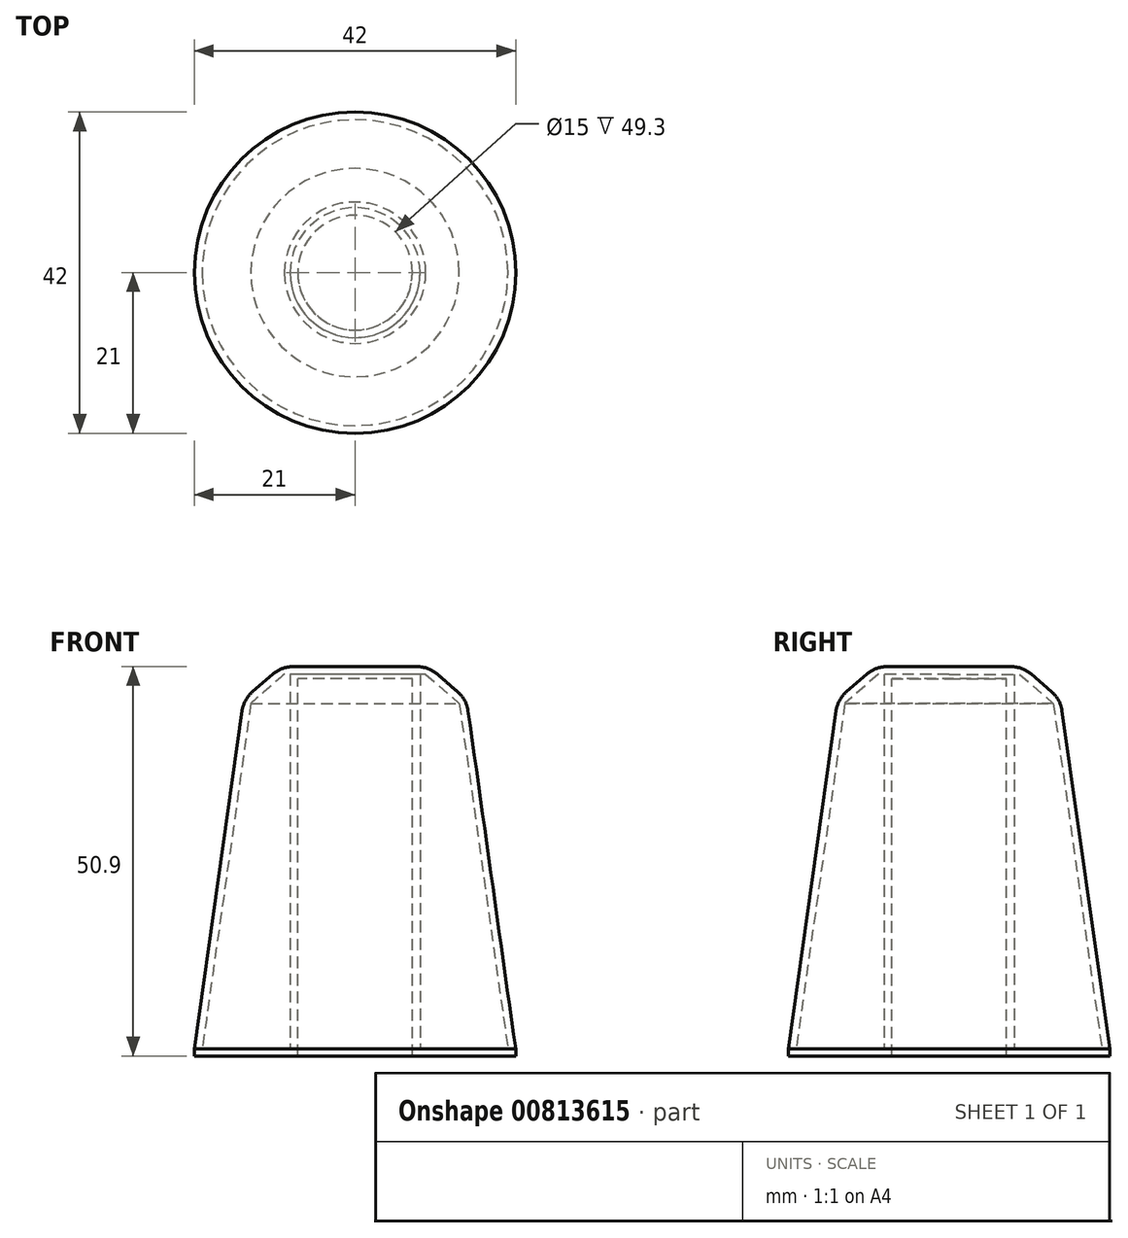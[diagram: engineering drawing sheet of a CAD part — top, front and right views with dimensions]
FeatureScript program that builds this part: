
annotation { "Feature Type Name" : "Feature", "Feature Type Description" : "" }
export const myFeature = defineFeature(function(context is Context, id is Id, definition is map)
    precondition{}
    {
        {
            assignVariable(context, id + "F0", {"name" : "Height", "anyValue" : 50});
        }
        {
            var Q0;
            Q0=qCreatedBy(makeId("Top.planeOp"),FACE);
            var sketch = newSketch(context, id + "F1", { "sketchPlane" : qUnion([Q0])});
            skCircle(sketch, "E0", {"center": v(0, 0) * mm, "radius": 21 * mm});
            skSolve(sketch);
        }
        {
            var Q0;
            Q0=qCreatedBy(makeId("Top.planeOp"),FACE);
            cPlane(context, id + "F2", {"entities" : qUnion([Q0]), "cplaneType" : CPlaneType.OFFSET, "offset" : (getVariable(context, 'Height')) * mm, "width" : 150 * mm, "height" : 150 * mm});
        }
        {
            var Q0;
            Q0=qCreatedBy(id+"F2.planeOp",FACE);
            var sketch = newSketch(context, id + "F3", { "sketchPlane" : qUnion([Q0])});
            skCircle(sketch, "E1", {"center": v(0, 0) * mm, "radius": 13.96 * mm});
            skSolve(sketch);
        }
        {
            var Q0;
            Q0=makeQuery(id+"F1.imprint","IMPRINT",FACE,{"disambiguationData":[TD([[makeQuery(id+"F1.imprint","IMPRINT",EDGE,{"derivedFrom":sQuery(id+"F1.wireOp",EDGE,"E0")}),1.0]])]});
            var Q1;
            Q1=makeQuery(id+"F3.imprint","IMPRINT",FACE,{"disambiguationData":[TD([[makeQuery(id+"F3.imprint","IMPRINT",EDGE,{"derivedFrom":sQuery(id+"F3.wireOp",EDGE,"E1")}),1.0]])]});
            loft(context, id + "F4", {"sheetProfilesArray" : [{ "sheetProfileEntities" : qUnion([Q0]) }, { "sheetProfileEntities" : qUnion([Q1]) }]});
        }
        {
            var Q0;
            Q0=makeQuery(id+"F4.opLoft","CAP_FACE",FACE,{"disambiguationData":[OSD([makeQuery(id+"F1.imprint","IMPRINT",FACE,{"disambiguationData":[TD([[makeQuery(id+"F1.imprint","IMPRINT",EDGE,{"derivedFrom":sQuery(id+"F1.wireOp",EDGE,"E0")}),1.0]])]})])],"isStart":true});
            var sketch = newSketch(context, id + "F5", { "sketchPlane" : qUnion([Q0])});
            skCircle(sketch, "E2", {"center": v(0, 0) * mm, "radius": 7.5 * mm});
            skSolve(sketch);
        }
        {
            var Q0;
            Q0=makeQuery(id+"F4.opLoft","MID_CAP_EDGE",EDGE,{"disambiguationData":[OSD([sQuery(id+"F3.wireOp",EDGE,"E1")])],"capPos":1.0});
            chamfer(context, id + "F6", {"entities" : qUnion([Q0]), "width" : 5 * mm, "tangentPropagation" : true});
        }
        {
            var Q0;
            Q0=makeQuery(id+"F4.opLoft","CAP_FACE",FACE,{"disambiguationData":[OSD([makeQuery(id+"F1.imprint","IMPRINT",FACE,{"disambiguationData":[TD([[makeQuery(id+"F1.imprint","IMPRINT",EDGE,{"derivedFrom":sQuery(id+"F1.wireOp",EDGE,"E0")}),1.0]])]})])],"isStart":true});
            shell(context, id + "F7", {"entities" : qUnion([Q0]), "thickness" : 1 * mm});
        }
        {
            var Q0;
            Q0=makeQuery(id+"F5.imprint","IMPRINT",FACE,{"disambiguationData":[TD([[makeQuery(id+"F5.imprint","IMPRINT",EDGE,{"derivedFrom":sQuery(id+"F5.wireOp",EDGE,"E2")}),-1.0]])]});
            extrude(context, id + "F8", {"entities" : qUnion([Q0]), "operationType" : NewBodyOperationType.ADD, "depth" : 0.9 * mm, "offsetDistance" : 25 * mm});
        }
        {
            var Q0;
            {var subQ0=sQuery(id+"F3.wireOp",EDGE,"E1");Q0=makeQuery(id+"F6.opChamfer","BLEND_EDGE",EDGE,{"blendedFrom":[makeQuery(id+"F4.opLoft","MID_CAP_EDGE",EDGE,{"disambiguationData":[OSD([subQ0])],"capPos":1.0}),makeQuery(id+"F4.opLoft","CAP_FACE",FACE,{"disambiguationData":[OSD([makeQuery(id+"F3.imprint","IMPRINT",FACE,{"disambiguationData":[TD([[makeQuery(id+"F3.imprint","IMPRINT",EDGE,{"derivedFrom":subQ0}),1.0]])]})])],"isStart":true})],"blendedInto":[makeQuery(id+"F4.opLoft","CAP_FACE",FACE,{"disambiguationData":[OSD([makeQuery(id+"F3.imprint","IMPRINT",FACE,{"disambiguationData":[TD([[makeQuery(id+"F3.imprint","IMPRINT",EDGE,{"derivedFrom":subQ0}),1.0]])]})])],"isStart":true})]});}
            var Q1;
            {var subQ0=sQuery(id+"F3.wireOp",EDGE,"E1");Q1=makeQuery(id+"F6.opChamfer","BLEND_EDGE",EDGE,{"blendedFrom":[makeQuery(id+"F4.opLoft","MID_CAP_EDGE",EDGE,{"disambiguationData":[OSD([subQ0])],"capPos":1.0}),makeQuery(id+"F4.opLoft","SWEPT_FACE",FACE,{"disambiguationData":[OSD([sQuery(id+"F1.wireOp",EDGE,"E0"),subQ0])]})],"blendedInto":[makeQuery(id+"F4.opLoft","SWEPT_FACE",FACE,{"disambiguationData":[OSD([sQuery(id+"F1.wireOp",EDGE,"E0"),subQ0])]})]});}
            fillet(context, id + "F9", {"entities" : qUnion([Q0, Q1]), "radius" : 4 * mm, "tangentPropagation" : true, "allowEdgeOverflow" : false});
        }
        {
            var Q0;
            Q0=makeQuery(id+"F8.opExtrude","CAP_FACE",FACE,{"disambiguationData":[OSD([sQuery(id+"F1.wireOp",EDGE,"E0"),sQuery(id+"F5.wireOp",EDGE,"E2")])],"isStart":false});
            var sketch = newSketch(context, id + "F10", { "sketchPlane" : qUnion([Q0])});
            skCircle(sketch, "E3.0", {"center": v(0, 0) * mm, "radius": 8.5 * mm});
            skCircle(sketch, "E4.0", {"center": v(0, 0) * mm, "radius": 16 * mm});
            skSolve(sketch);
        }
        {
            var Q0;
            Q0=makeQuery(id+"F10.imprint","IMPRINT",FACE,{"disambiguationData":[TD([[makeQuery(id+"F10.imprint","IMPRINT",EDGE,{"derivedFrom":sQuery(id+"F10.wireOp",EDGE,"E3.0")}),1.0]])]});
            var Q1;
            Q1=makeQuery(id+"F7.opShell","OFFSET_FACE",FACE,{"disambiguationData":[OSD([makeQuery(id+"F3.imprint","IMPRINT",FACE,{"disambiguationData":[TD([[makeQuery(id+"F3.imprint","IMPRINT",EDGE,{"derivedFrom":sQuery(id+"F3.wireOp",EDGE,"E1")}),1.0]])]})])]});
            extrude(context, id + "F11", {"entities" : qUnion([Q0]), "operationType" : NewBodyOperationType.ADD, "endBound" : BoundingType.UP_TO_SURFACE, "oppositeDirection" : true, "depth" : 25 * mm, "endBoundEntityFace" : qUnion([Q1]), "offsetDistance" : 25 * mm});
        }
        {
            var Q0;
            {var subQ0=sQuery(id+"F5.wireOp",EDGE,"E2");Q0=makeQuery(id+"F11.boolean.opBoolean","SPLIT",FACE,{"disambiguationData":[TD([makeQuery(id+"F8.opExtrude","SWEPT_FACE",FACE,{"disambiguationData":[OSD([subQ0])]})])],"derivedFrom":makeQuery(id+"F7.opShell","OFFSET_FACE",FACE,{"disambiguationData":[OSD([makeQuery(id+"F3.imprint","IMPRINT",FACE,{"disambiguationData":[TD([[makeQuery(id+"F3.imprint","IMPRINT",EDGE,{"derivedFrom":sQuery(id+"F3.wireOp",EDGE,"E1")}),1.0]])]})])]})});}
            extrude(context, id + "F12", {"entities" : qUnion([Q0]), "operationType" : NewBodyOperationType.ADD, "depth" : 0.6 * mm, "offsetDistance" : 25 * mm});
        }
    });
